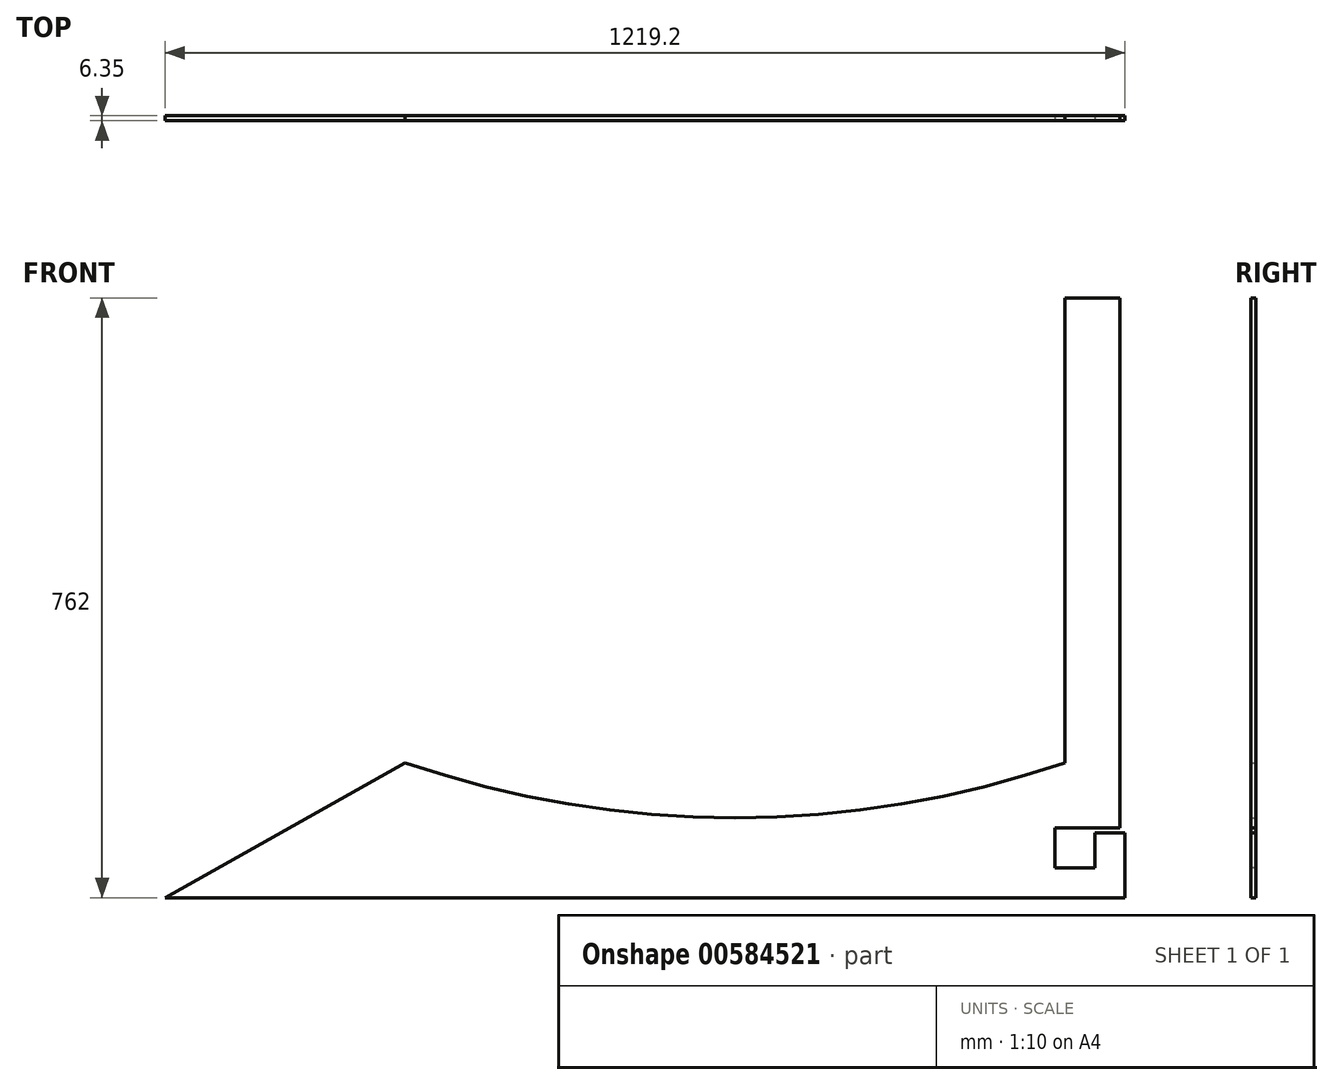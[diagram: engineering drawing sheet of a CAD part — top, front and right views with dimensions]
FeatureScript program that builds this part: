
annotation { "Feature Type Name" : "Feature", "Feature Type Description" : "" }
export const myFeature = defineFeature(function(context is Context, id is Id, definition is map)
    precondition{}
    {
        {
            var Q0;
            Q0=qCreatedBy(makeId("Front.planeOp"),FACE);
            var sketch = newSketch(context, id + "F0", { "sketchPlane" : qUnion([Q0])});
            skLineSegment(sketch, "E0", {"start": v(0, 0) * mm, "end": v(1219.2, 0) * mm});
            skLineSegment(sketch, "E1", {"start": v(1219.2, 0) * mm, "end": v(1219.2, 762) * mm});
            skLineSegment(sketch, "E2", {"start": v(1219.2, 762) * mm, "end": v(1143, 762) * mm});
            skLineSegment(sketch, "E3", {"start": v(1143, 762) * mm, "end": v(1143, 101.6) * mm});
            skLineSegment(sketch, "E4", {"start": v(1143, 101.6) * mm, "end": v(304.8, 101.6) * mm});
            skLineSegment(sketch, "E5", {"start": v(304.8, 101.6) * mm, "end": v(304.8, 171.45) * mm});
            skLineSegment(sketch, "E6", {"start": v(304.8, 171.45) * mm, "end": v(0, 0) * mm});
            skLineSegment(sketch, "E7", {"start": v(304.8, 171.45) * mm, "end": v(1143, 171.45) * mm, "construction": true});
            skLineSegment(sketch, "E8", {"start": v(304.8, 101.6) * mm, "end": v(723.9, 101.6) * mm});
            skArc(sketch, "E9", {"start": v(304.8, 171.45) * mm, "mid": v(723.9, 101.6) * mm, "end": v(1143, 171.45) * mm});
            skLineSegment(sketch, "E10.bottom", {"start": v(496.64, 358.87) * mm, "end": v(660.93, 358.87) * mm});
            skLineSegment(sketch, "E10.top", {"start": v(496.64, 443.75) * mm, "end": v(660.93, 443.75) * mm});
            skLineSegment(sketch, "E10.left", {"start": v(496.64, 358.87) * mm, "end": v(496.64, 443.75) * mm});
            skLineSegment(sketch, "E10.right", {"start": v(660.93, 358.87) * mm, "end": v(660.93, 443.75) * mm});
            skLineSegment(sketch, "E11", {"start": v(304.8, 171.45) * mm, "end": v(268.48, 135.93) * mm});
            skLineSegment(sketch, "E12", {"start": v(304.8, 171.45) * mm, "end": v(340.32, 135.13) * mm});
            skLineSegment(sketch, "E13", {"start": v(340.32, 135.13) * mm, "end": v(304, 99.61) * mm});
            skLineSegment(sketch, "E14", {"start": v(304, 99.61) * mm, "end": v(268.48, 135.93) * mm});
            skSolve(sketch);
        }
        {
            var Q0;
            Q0=makeQuery(id+"F0.imprint","IMPRINT",FACE,{"disambiguationData":[TD([[makeQuery(id+"F0.imprint","IMPRINT",EDGE,{"derivedFrom":sQuery(id+"F0.wireOp",EDGE,"E0")}),1.0]])]});
            var Q1;
            {var subQ5=sQuery(id+"F0.wireOp",EDGE,"E12");Q1=makeQuery(id+"F0.imprint","IMPRINT",FACE,{"disambiguationData":[TD([[makeQuery(id+"F0.imprint","IMPRINT",EDGE,{"derivedFrom":subQ5}),1.0]])]});}
            var Q2;
            {var subQ0=sQuery(id+"F0.wireOp",EDGE,"E4");Q2=makeQuery(id+"F0.imprint","IMPRINT",FACE,{"disambiguationData":[TD([[makeQuery(id+"F0.imprint","IMPRINT",EDGE,{"derivedFrom":subQ0}),-1.0]])]});}
            var Q3;
            {var subQ4=sQuery(id+"F0.wireOp",EDGE,"E5");Q3=makeQuery(id+"F0.imprint","IMPRINT",FACE,{"disambiguationData":[TD([[makeQuery(id+"F0.imprint","IMPRINT",EDGE,{"derivedFrom":subQ4}),1.0]])]});}
            var Q4;
            {var subQ0=sQuery(id+"F0.wireOp",EDGE,"E5");Q4=makeQuery(id+"F0.imprint","IMPRINT",FACE,{"disambiguationData":[TD([[makeQuery(id+"F0.imprint","IMPRINT",EDGE,{"derivedFrom":subQ0}),-1.0]])]});}
            extrude(context, id + "F1", {"entities" : qUnion([Q0, Q1, Q2, Q3, Q4]), "depth" : 6.35 * mm, "offsetDistance" : 25.4 * mm});
        }
        {
            var Q0;
            Q0=makeQuery(id+"F1.opExtrude","CAP_FACE",FACE,{"disambiguationData":[OSD([sQuery(id+"F0.wireOp",EDGE,"E0"),sQuery(id+"F0.wireOp",EDGE,"E1"),sQuery(id+"F0.wireOp",EDGE,"E2"),sQuery(id+"F0.wireOp",EDGE,"E3"),sQuery(id+"F0.wireOp",EDGE,"E6"),sQuery(id+"F0.wireOp",EDGE,"E9")])],"isStart":false});
            var sketch = newSketch(context, id + "F2", { "sketchPlane" : qUnion([Q0])});
            skLineSegment(sketch, "E15.bottom", {"start": v(1130.3, 38.1) * mm, "end": v(1181.1, 38.1) * mm});
            skLineSegment(sketch, "E15.top", {"start": v(1130.3, 88.9) * mm, "end": v(1181.1, 88.9) * mm});
            skLineSegment(sketch, "E15.left", {"start": v(1130.3, 38.1) * mm, "end": v(1130.3, 88.9) * mm});
            skLineSegment(sketch, "E15.right", {"start": v(1181.1, 38.1) * mm, "end": v(1181.1, 88.9) * mm});
            skLineSegment(sketch, "E16", {"start": v(1219.2, 762) * mm, "end": v(1212.85, 762) * mm});
            skLineSegment(sketch, "E17", {"start": v(1212.85, 762) * mm, "end": v(1212.85, 88.9) * mm});
            skLineSegment(sketch, "E18", {"start": v(1212.85, 88.9) * mm, "end": v(1219.2, 88.9) * mm});
            skLineSegment(sketch, "E19", {"start": v(1219.2, 88.9) * mm, "end": v(1219.2, 762) * mm});
            skLineSegment(sketch, "E20", {"start": v(1219.2, 88.9) * mm, "end": v(1219.2, 82.55) * mm});
            skLineSegment(sketch, "E21", {"start": v(1219.2, 82.55) * mm, "end": v(1181.1, 82.55) * mm});
            skLineSegment(sketch, "E22", {"start": v(1181.1, 82.55) * mm, "end": v(1181.1, 88.9) * mm});
            skLineSegment(sketch, "E23", {"start": v(1181.1, 88.9) * mm, "end": v(1212.85, 88.9) * mm});
            skSolve(sketch);
        }
        {
            var Q0;
            Q0=makeQuery(id+"F2.imprint","IMPRINT",FACE,{"disambiguationData":[TD([[makeQuery(id+"F2.imprint","IMPRINT",EDGE,{"derivedFrom":sQuery(id+"F2.wireOp",EDGE,"E15.bottom")}),1.0]])]});
            var Q1;
            Q1=makeQuery(id+"F2.imprint","IMPRINT",FACE,{"disambiguationData":[TD([[makeQuery(id+"F2.imprint","IMPRINT",EDGE,{"derivedFrom":sQuery(id+"F2.wireOp",EDGE,"E16")}),1.0]])]});
            var Q2;
            Q2=makeQuery(id+"F2.imprint","IMPRINT",FACE,{"disambiguationData":[TD([[makeQuery(id+"F2.imprint","IMPRINT",EDGE,{"derivedFrom":sQuery(id+"F2.wireOp",EDGE,"E18")}),-1.0]])]});
            extrude(context, id + "F3", {"entities" : qUnion([Q0, Q1, Q2]), "operationType" : NewBodyOperationType.REMOVE, "oppositeDirection" : true, "depth" : 25.4 * mm, "offsetDistance" : 25.4 * mm});
        }
    });
